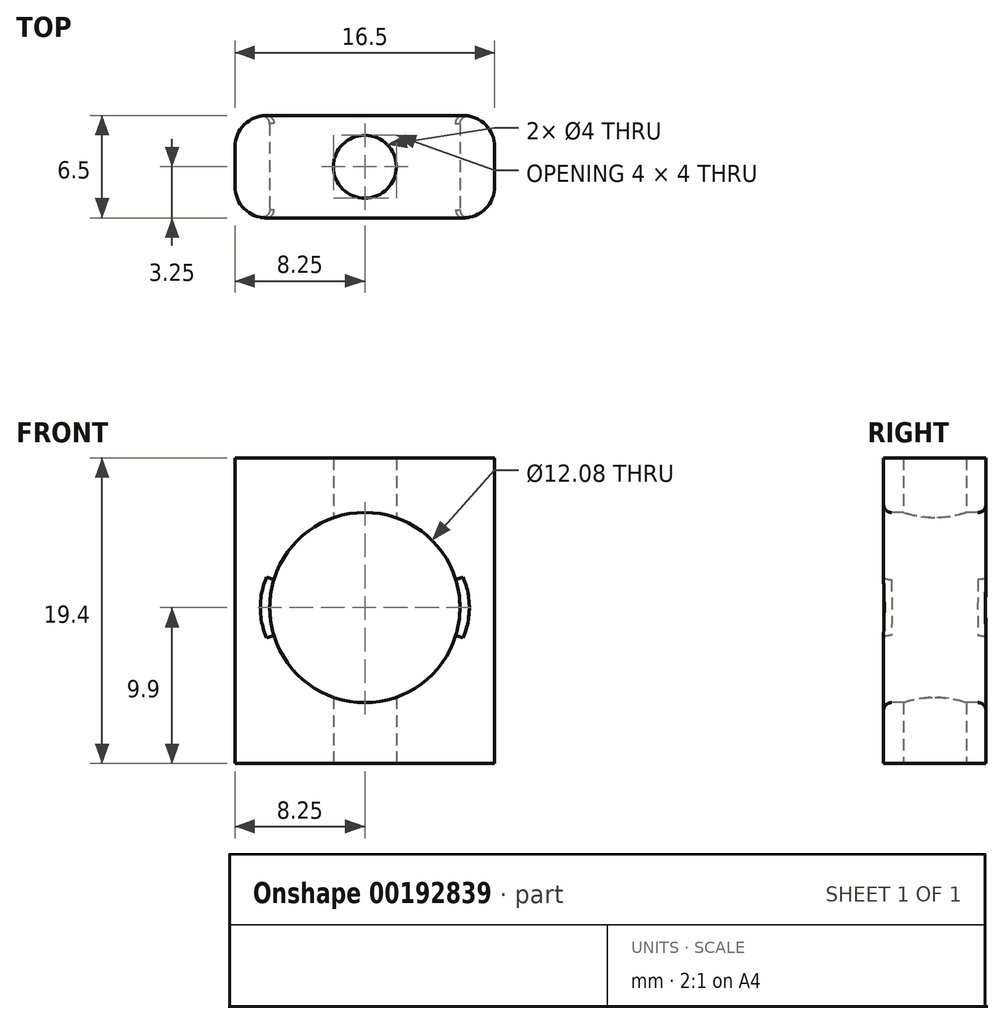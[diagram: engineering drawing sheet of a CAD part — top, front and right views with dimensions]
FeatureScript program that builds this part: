
annotation { "Feature Type Name" : "Feature", "Feature Type Description" : "" }
export const myFeature = defineFeature(function(context is Context, id is Id, definition is map)
    precondition{}
    {
        {
            var Q0;
            Q0=qCreatedBy(makeId("Top.planeOp"),FACE);
            var sketch = newSketch(context, id + "F0", { "sketchPlane" : qUnion([Q0])});
            skLineSegment(sketch, "E0.bottom", {"start": v(8.25, 3.25) * mm, "end": v(-8.25, 3.25) * mm});
            skLineSegment(sketch, "E0.top", {"start": v(8.25, -3.25) * mm, "end": v(-8.25, -3.25) * mm});
            skLineSegment(sketch, "E0.left", {"start": v(8.25, 3.25) * mm, "end": v(8.25, -3.25) * mm});
            skLineSegment(sketch, "E0.right", {"start": v(-8.25, 3.25) * mm, "end": v(-8.25, -3.25) * mm});
            skPoint(sketch, "E0.middle", {"position": v(0, 0) * mm});
            skCircle(sketch, "E1", {"center": v(0, 0) * mm, "radius": 2 * mm});
            skSolve(sketch);
        }
        {
            var Q0;
            Q0 = qSketchRegion(id + "F0", true);
            extrude(context, id + "F1", {"entities" : qUnion([Q0]), "depth" : 19.4 * mm});
        }
        {
            var Q0;
            Q0=makeQuery(id+"F1.opExtrude","SWEPT_FACE",FACE,{"disambiguationData":[OSD([sQuery(id+"F0.wireOp",EDGE,"E0.top")])]});
            var sketch = newSketch(context, id + "F2", { "sketchPlane" : qUnion([Q0])});
            skCircle(sketch, "E2", {"center": v(0, 9.9) * mm, "radius": 6.04 * mm});
            skPoint(sketch, "E2.centerSnap0", {"position": v(0, 19.4) * mm});
            skSolve(sketch);
        }
        {
            var Q0;
            Q0=makeQuery(id+"F2.imprint","IMPRINT",FACE,{"disambiguationData":[TD([[makeQuery(id+"F2.imprint","IMPRINT",EDGE,{"derivedFrom":sQuery(id+"F2.wireOp",EDGE,"E2")}),1.0]])]});
            extrude(context, id + "F3", {"entities" : qUnion([Q0]), "operationType" : NewBodyOperationType.REMOVE, "oppositeDirection" : true, "depth" : 25 * mm, "hasSecondDirection" : true, "secondDirectionOppositeDirection" : false, "secondDirectionDepth" : 25 * mm});
        }
        {
            var Q0;
            Q0 = qSketchRegion(id + "F0", true);
            var Q1;
            Q1=sQuery(id+"F0.wireOp",EDGE,"E1");
            extrude(context, id + "F4", {"entities" : qUnion([Q0]), "operationType" : NewBodyOperationType.REMOVE, "surfaceEntities" : qUnion([Q1]), "oppositeDirection" : true, "depth" : 3 * mm});
        }
        {
            var Q0;
            Q0=makeQuery(id+"F1.opExtrude","SWEPT_EDGE",EDGE,{"disambiguationData":[OSD([sQuery(id+"F0.wireOp",EDGE,"E0.top"),sQuery(id+"F0.wireOp",EDGE,"E0.left")])]});
            var Q1;
            Q1=makeQuery(id+"F1.opExtrude","SWEPT_EDGE",EDGE,{"disambiguationData":[OSD([sQuery(id+"F0.wireOp",EDGE,"E0.top"),sQuery(id+"F0.wireOp",EDGE,"E0.right")])]});
            var Q2;
            Q2=makeQuery(id+"F1.opExtrude","SWEPT_EDGE",EDGE,{"disambiguationData":[OSD([sQuery(id+"F0.wireOp",EDGE,"E0.bottom"),sQuery(id+"F0.wireOp",EDGE,"E0.right")])]});
            var Q3;
            Q3=makeQuery(id+"F1.opExtrude","SWEPT_EDGE",EDGE,{"disambiguationData":[OSD([sQuery(id+"F0.wireOp",EDGE,"E0.bottom"),sQuery(id+"F0.wireOp",EDGE,"E0.left")])]});
            fillet(context, id + "F5", {"entities" : qUnion([Q0, Q1, Q2, Q3]), "radius" : 2 * mm, "tangentPropagation" : true, "allowEdgeOverflow" : false});
        }
        {
            var Q0;
            Q0=makeQuery(id+"F3.boolean.opBoolean","INTERSECT",EDGE,{"derivedFrom":[makeQuery(id+"F1.opExtrude","SWEPT_FACE",FACE,{"disambiguationData":[OSD([sQuery(id+"F0.wireOp",EDGE,"E0.top")])]}),makeQuery(id+"F3.opExtrude","SWEPT_FACE",FACE,{"disambiguationData":[OSD([sQuery(id+"F2.wireOp",EDGE,"E2")])]})]});
            var Q1;
            Q1=makeQuery(id+"F3.boolean.opBoolean","INTERSECT",EDGE,{"derivedFrom":[makeQuery(id+"F1.opExtrude","SWEPT_FACE",FACE,{"disambiguationData":[OSD([sQuery(id+"F0.wireOp",EDGE,"E0.bottom")])]}),makeQuery(id+"F3.opExtrude","SWEPT_FACE",FACE,{"disambiguationData":[OSD([sQuery(id+"F2.wireOp",EDGE,"E2")])]})]});
            fillet(context, id + "F6", {"entities" : qUnion([Q0, Q1]), "radius" : 0.5 * mm, "tangentPropagation" : true, "allowEdgeOverflow" : false});
        }
    });
